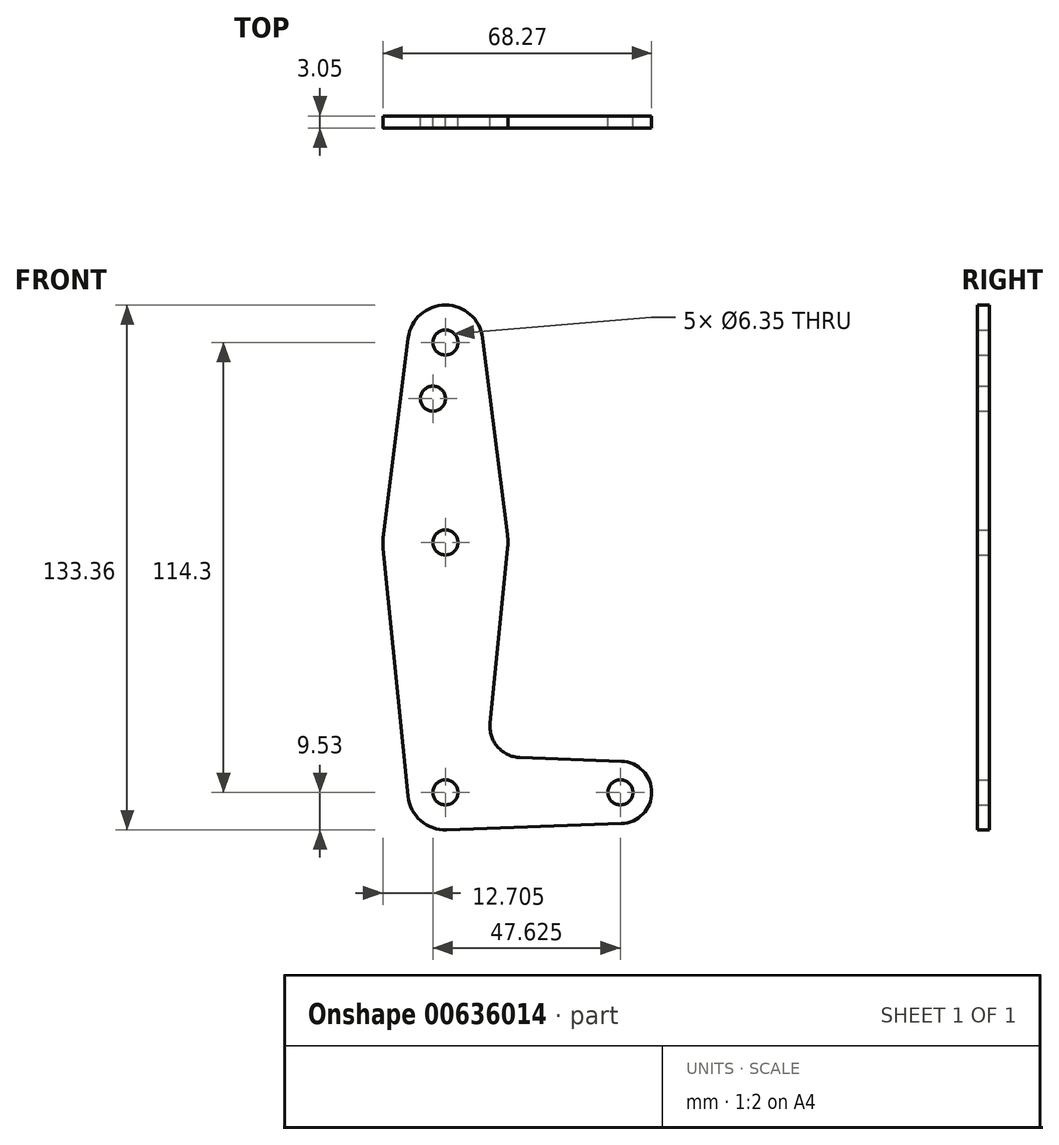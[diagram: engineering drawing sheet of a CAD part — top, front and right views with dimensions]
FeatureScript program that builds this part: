
annotation { "Feature Type Name" : "Feature", "Feature Type Description" : "" }
export const myFeature = defineFeature(function(context is Context, id is Id, definition is map)
    precondition{}
    {
        {
            var Q0;
            Q0=qCreatedBy(makeId("Front.planeOp"),FACE);
            var sketch = newSketch(context, id + "F0", { "sketchPlane" : qUnion([Q0])});
            skLineSegment(sketch, "E0", {"start": v(0, 0) * mm, "end": v(0, -114.3) * mm, "construction": true});
            skLineSegment(sketch, "E1", {"start": v(0, -114.3) * mm, "end": v(44.45, -114.3) * mm, "construction": true});
            skCircle(sketch, "E2", {"center": v(0, -50.8) * mm, "radius": 15.88 * mm});
            skCircle(sketch, "E3", {"center": v(0, -114.3) * mm, "radius": 9.53 * mm});
            skCircle(sketch, "E4", {"center": v(44.45, -114.3) * mm, "radius": 7.94 * mm});
            skCircle(sketch, "E5", {"center": v(0, 0) * mm, "radius": 9.53 * mm});
            skLineSegment(sketch, "E6", {"start": v(-15.8, -52.39) * mm, "end": v(-9.48, -115.25) * mm});
            skLineSegment(sketch, "E7", {"start": v(15.8, -52.39) * mm, "end": v(11.34, -96.7) * mm});
            skLineSegment(sketch, "E8", {"start": v(0.34, -123.82) * mm, "end": v(44.73, -122.23) * mm});
            skLineSegment(sketch, "E9", {"start": v(18.97, -105.45) * mm, "end": v(44.73, -106.37) * mm});
            skLineSegment(sketch, "E10", {"start": v(-9.45, 1.2) * mm, "end": v(-15.75, -48.82) * mm});
            skLineSegment(sketch, "E11", {"start": v(9.45, 1.2) * mm, "end": v(15.75, -48.82) * mm});
            skCircle(sketch, "E12", {"center": v(0, 0) * mm, "radius": 3.18 * mm});
            skCircle(sketch, "E13", {"center": v(0, -50.8) * mm, "radius": 3.18 * mm});
            skCircle(sketch, "E14", {"center": v(0, -114.3) * mm, "radius": 3.18 * mm});
            skCircle(sketch, "E15", {"center": v(-3.18, -14.27) * mm, "radius": 3.18 * mm});
            skCircle(sketch, "E16", {"center": v(44.45, -114.3) * mm, "radius": 3.18 * mm});
            skArc(sketch, "E17.filletArc", {"start": v(11.34, -96.7) * mm, "mid": v(13.26, -102.73) * mm, "end": v(18.97, -105.45) * mm});
            skSolve(sketch);
        }
        {
            var Q0;
            Q0 = qSketchRegion(id + "F0", true);
            extrude(context, id + "F1", {"entities" : qUnion([Q0]), "depth" : 3.05 * mm, "offsetDistance" : 25.4 * mm});
        }
    });
